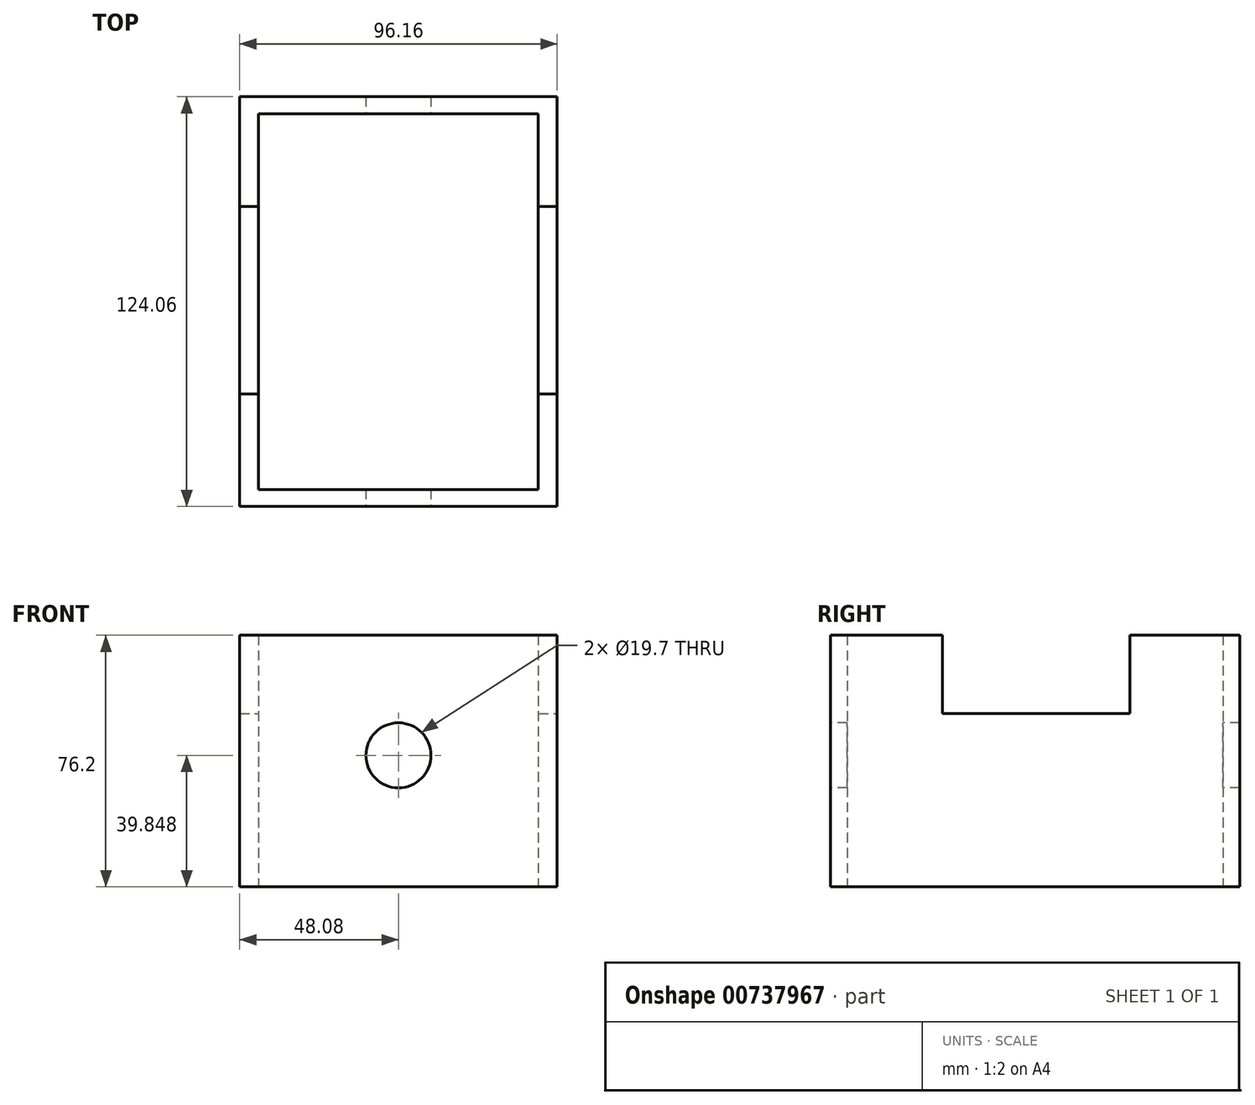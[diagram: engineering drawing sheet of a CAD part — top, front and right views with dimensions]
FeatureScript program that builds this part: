
annotation { "Feature Type Name" : "Feature", "Feature Type Description" : "" }
export const myFeature = defineFeature(function(context is Context, id is Id, definition is map)
    precondition{}
    {
        {
            var Q0;
            Q0=qCreatedBy(makeId("Top.planeOp"),FACE);
            var sketch = newSketch(context, id + "F0", { "sketchPlane" : qUnion([Q0])});
            skLineSegment(sketch, "E0.bottom", {"start": v(48.08, 62.03) * mm, "end": v(-48.08, 62.03) * mm});
            skLineSegment(sketch, "E0.top", {"start": v(48.08, -62.03) * mm, "end": v(-48.08, -62.03) * mm});
            skLineSegment(sketch, "E0.left", {"start": v(48.08, 62.03) * mm, "end": v(48.08, -62.03) * mm});
            skLineSegment(sketch, "E0.right", {"start": v(-48.08, 62.03) * mm, "end": v(-48.08, -62.03) * mm});
            skPoint(sketch, "E0.middle", {"position": v(0, 0) * mm});
            skLineSegment(sketch, "E1.bottom", {"start": v(42.36, 56.86) * mm, "end": v(-42.36, 56.86) * mm});
            skLineSegment(sketch, "E1.top", {"start": v(42.36, -56.86) * mm, "end": v(-42.36, -56.86) * mm});
            skLineSegment(sketch, "E1.left", {"start": v(42.36, 56.86) * mm, "end": v(42.36, -56.86) * mm});
            skLineSegment(sketch, "E1.right", {"start": v(-42.36, 56.86) * mm, "end": v(-42.36, -56.86) * mm});
            skSolve(sketch);
        }
        {
            var Q0;
            Q0 = qSketchRegion(id + "F0", true);
            extrude(context, id + "F1", {"entities" : qUnion([Q0]), "depth" : 76.2 * mm, "offsetDistance" : 25.4 * mm});
        }
        {
            var Q0;
            Q0=makeQuery(id+"F1.opExtrude","SWEPT_FACE",FACE,{"disambiguationData":[OSD([sQuery(id+"F0.wireOp",EDGE,"E0.top")])]});
            var sketch = newSketch(context, id + "F2", { "sketchPlane" : qUnion([Q0])});
            skCircle(sketch, "E2", {"center": v(0, 39.85) * mm, "radius": 9.85 * mm});
            skSolve(sketch);
        }
        {
            var Q0;
            Q0 = qSketchRegion(id + "F2", true);
            extrude(context, id + "F3", {"entities" : qUnion([Q0]), "operationType" : NewBodyOperationType.REMOVE, "oppositeDirection" : true, "depth" : 127 * mm, "offsetDistance" : 25.4 * mm});
        }
        {
            var Q0;
            Q0=makeQuery(id+"F1.opExtrude","SWEPT_FACE",FACE,{"disambiguationData":[OSD([sQuery(id+"F0.wireOp",EDGE,"E0.left")])]});
            var sketch = newSketch(context, id + "F4", { "sketchPlane" : qUnion([Q0])});
            skLineSegment(sketch, "E3.bottom", {"start": v(-28.02, 76.2) * mm, "end": v(28.75, 76.2) * mm});
            skLineSegment(sketch, "E3.top", {"start": v(-28.02, 52.48) * mm, "end": v(28.75, 52.48) * mm});
            skLineSegment(sketch, "E3.left", {"start": v(-28.02, 76.2) * mm, "end": v(-28.02, 52.48) * mm});
            skLineSegment(sketch, "E3.right", {"start": v(28.75, 76.2) * mm, "end": v(28.75, 52.48) * mm});
            skSolve(sketch);
        }
        {
            var Q0;
            Q0 = qSketchRegion(id + "F4", true);
            extrude(context, id + "F5", {"entities" : qUnion([Q0]), "operationType" : NewBodyOperationType.REMOVE, "oppositeDirection" : true, "depth" : 127 * mm, "offsetDistance" : 25.4 * mm});
        }
    });
